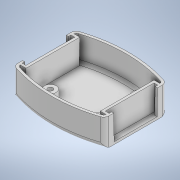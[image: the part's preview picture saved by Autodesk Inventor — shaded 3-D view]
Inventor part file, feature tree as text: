
AUTODESK INVENTOR PART (.ipt)
format: ipt  version: 2020 (Build 240168000, 168)  size: 278,016 bytes
history: native  units: in
note: dims shown in document units (in); Inventor stores cm internally (conversion verified against a paired STEP export)
features: extrude x4, sketch x3, fillet x1, shell x1
ambient origin geometry x8: Origin, YZ Plane, XZ Plane, XY Plane, X Axis, Y Axis, Z Axis, Center Point
bodies: Body1 (feature_tree)
feature tree (9):
  extrude  "Extrusion5"  Depth=2.165in
  sketch  "Sketch6"  dims[d42=0.187in d43=2.165in d51=0.591in]
  extrude  "Extrusion6"  Depth=2.165in
  fillet  "Fillet5"  Radius=0.591in
  extrude  "Extrusion7"  Depth=0.197in
  shell  "Shell2"  Thickness=0.06in
  extrude  "Extrusion8"  Depth=0.197in
  sketch  "Sketch1"  dims[d40=0.187in d41=2.165in]
  sketch  "Sketch7"  dims[d52=0.0in d53=0.3985in d54=0.06in d55=0.06in d56=0.073in d57=1.142in d58=0.073in d59=0.06in d60=0.06in d61=2.165in d62=0.3985in d63=0.06in d64=0.06in d65=0.073in d66=1.142in d67=0.073in d68=0.06in d69=0.06in d70=1.445in d71=0.187in d72=1.445in d73=1.445in d74=0.06in d75=0.0in d76=0.125in d77=0.591in d78=0.0053in d79=0.06in d80=1.819in d81=0.9095in d82=1.0825in d83=0.7025in d84=0.6625in d86=1.325in d87=1.405in d88=0.1in d89=0.12in d92=0.925in d93=1.16in d94=0.119in d95=0.276in d98=0.197in d99=0.0in d100=0.4077in d101=0.1791in]
